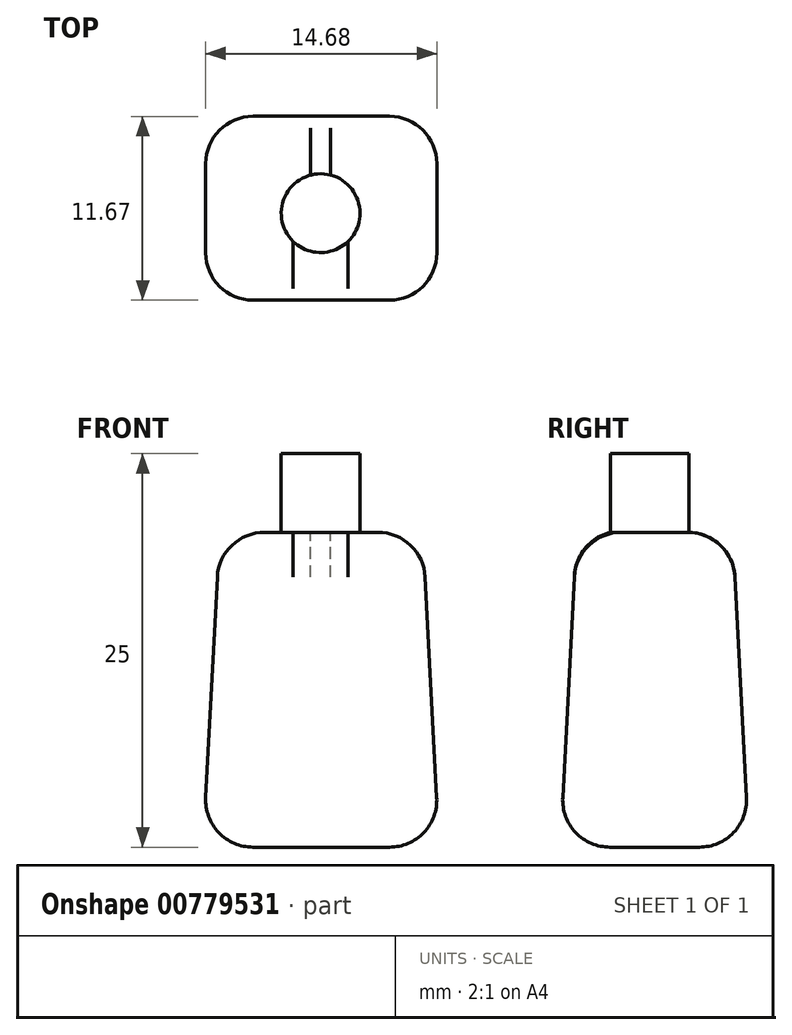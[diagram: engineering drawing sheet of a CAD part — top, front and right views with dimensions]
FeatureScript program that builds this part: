
annotation { "Feature Type Name" : "Feature", "Feature Type Description" : "" }
export const myFeature = defineFeature(function(context is Context, id is Id, definition is map)
    precondition{}
    {
        {
            var Q0;
            Q0=qCreatedBy(makeId("Top.planeOp"),FACE);
            var sketch = newSketch(context, id + "F0", { "sketchPlane" : qUnion([Q0])});
            skLineSegment(sketch, "E0.bottom", {"start": v(-7.46, 6.31) * mm, "end": v(7.54, 6.31) * mm});
            skLineSegment(sketch, "E0.top", {"start": v(-7.46, -5.69) * mm, "end": v(7.54, -5.69) * mm});
            skLineSegment(sketch, "E0.left", {"start": v(-7.46, 6.31) * mm, "end": v(-7.46, -5.69) * mm});
            skLineSegment(sketch, "E0.right", {"start": v(7.54, 6.31) * mm, "end": v(7.54, -5.69) * mm});
            skSolve(sketch);
        }
        {
            var Q0;
            Q0 = qSketchRegion(id + "F0", true);
            extrude(context, id + "F1", {"entities" : qUnion([Q0]), "depth" : 20 * mm, "offsetDistance" : 25 * mm, "hasDraft" : true, "draftAngle" : 3 * degree, "draftPullDirection" : true});
        }
        {
            var Q0;
            Q0=makeQuery(id+"F1.opExtrude","CAP_FACE",FACE,{"disambiguationData":[OSD([sQuery(id+"F0.wireOp",EDGE,"E0.bottom"),sQuery(id+"F0.wireOp",EDGE,"E0.top"),sQuery(id+"F0.wireOp",EDGE,"E0.left"),sQuery(id+"F0.wireOp",EDGE,"E0.right")])],"isStart":false});
            var sketch = newSketch(context, id + "F2", { "sketchPlane" : qUnion([Q0])});
            skCircle(sketch, "E1", {"center": v(0, 0) * mm, "radius": 2.5 * mm});
            skSolve(sketch);
        }
        {
            var Q0;
            Q0 = qSketchRegion(id + "F2", true);
            extrude(context, id + "F3", {"entities" : qUnion([Q0]), "operationType" : NewBodyOperationType.ADD, "depth" : 5 * mm, "offsetDistance" : 25 * mm});
        }
        {
            var Q0;
            Q0=makeQuery(id+"F1.opExtrude","CAP_EDGE",EDGE,{"disambiguationData":[OSD([sQuery(id+"F0.wireOp",EDGE,"E0.bottom")])],"isStart":false});
            var Q1;
            Q1=makeQuery(id+"F1.opExtrude","CAP_EDGE",EDGE,{"disambiguationData":[OSD([sQuery(id+"F0.wireOp",EDGE,"E0.bottom")])],"isStart":true});
            var Q2;
            Q2=makeQuery(id+"F1.opExtrude","SWEPT_EDGE",EDGE,{"disambiguationData":[OSD([sQuery(id+"F0.wireOp",EDGE,"E0.bottom"),sQuery(id+"F0.wireOp",EDGE,"E0.left")])]});
            var Q3;
            Q3=makeQuery(id+"F1.opExtrude","SWEPT_FACE",FACE,{"disambiguationData":[OSD([sQuery(id+"F0.wireOp",EDGE,"E0.bottom")])]});
            var Q4;
            Q4=makeQuery(id+"F1.opExtrude","SWEPT_EDGE",EDGE,{"disambiguationData":[OSD([sQuery(id+"F0.wireOp",EDGE,"E0.top"),sQuery(id+"F0.wireOp",EDGE,"E0.left")])]});
            var Q5;
            Q5=makeQuery(id+"F1.opExtrude","CAP_EDGE",EDGE,{"disambiguationData":[OSD([sQuery(id+"F0.wireOp",EDGE,"E0.left")])],"isStart":false});
            var Q6;
            Q6=makeQuery(id+"F1.opExtrude","CAP_EDGE",EDGE,{"disambiguationData":[OSD([sQuery(id+"F0.wireOp",EDGE,"E0.left")])],"isStart":true});
            var Q7;
            Q7=makeQuery(id+"F1.opExtrude","CAP_EDGE",EDGE,{"disambiguationData":[OSD([sQuery(id+"F0.wireOp",EDGE,"E0.top")])],"isStart":false});
            var Q8;
            Q8=makeQuery(id+"F1.opExtrude","CAP_EDGE",EDGE,{"disambiguationData":[OSD([sQuery(id+"F0.wireOp",EDGE,"E0.top")])],"isStart":true});
            var Q9;
            Q9=makeQuery(id+"F1.opExtrude","SWEPT_EDGE",EDGE,{"disambiguationData":[OSD([sQuery(id+"F0.wireOp",EDGE,"E0.top"),sQuery(id+"F0.wireOp",EDGE,"E0.right")])]});
            var Q10;
            Q10=makeQuery(id+"F1.opExtrude","CAP_EDGE",EDGE,{"disambiguationData":[OSD([sQuery(id+"F0.wireOp",EDGE,"E0.right")])],"isStart":false});
            var Q11;
            Q11=makeQuery(id+"F1.opExtrude","CAP_EDGE",EDGE,{"disambiguationData":[OSD([sQuery(id+"F0.wireOp",EDGE,"E0.right")])],"isStart":true});
            fillet(context, id + "F4", {"entities" : qUnion([Q0, Q1, Q2, Q3, Q4, Q5, Q6, Q7, Q8, Q9, Q10, Q11]), "radius" : 3 * mm, "tangentPropagation" : true, "allowEdgeOverflow" : false});
        }
    });
